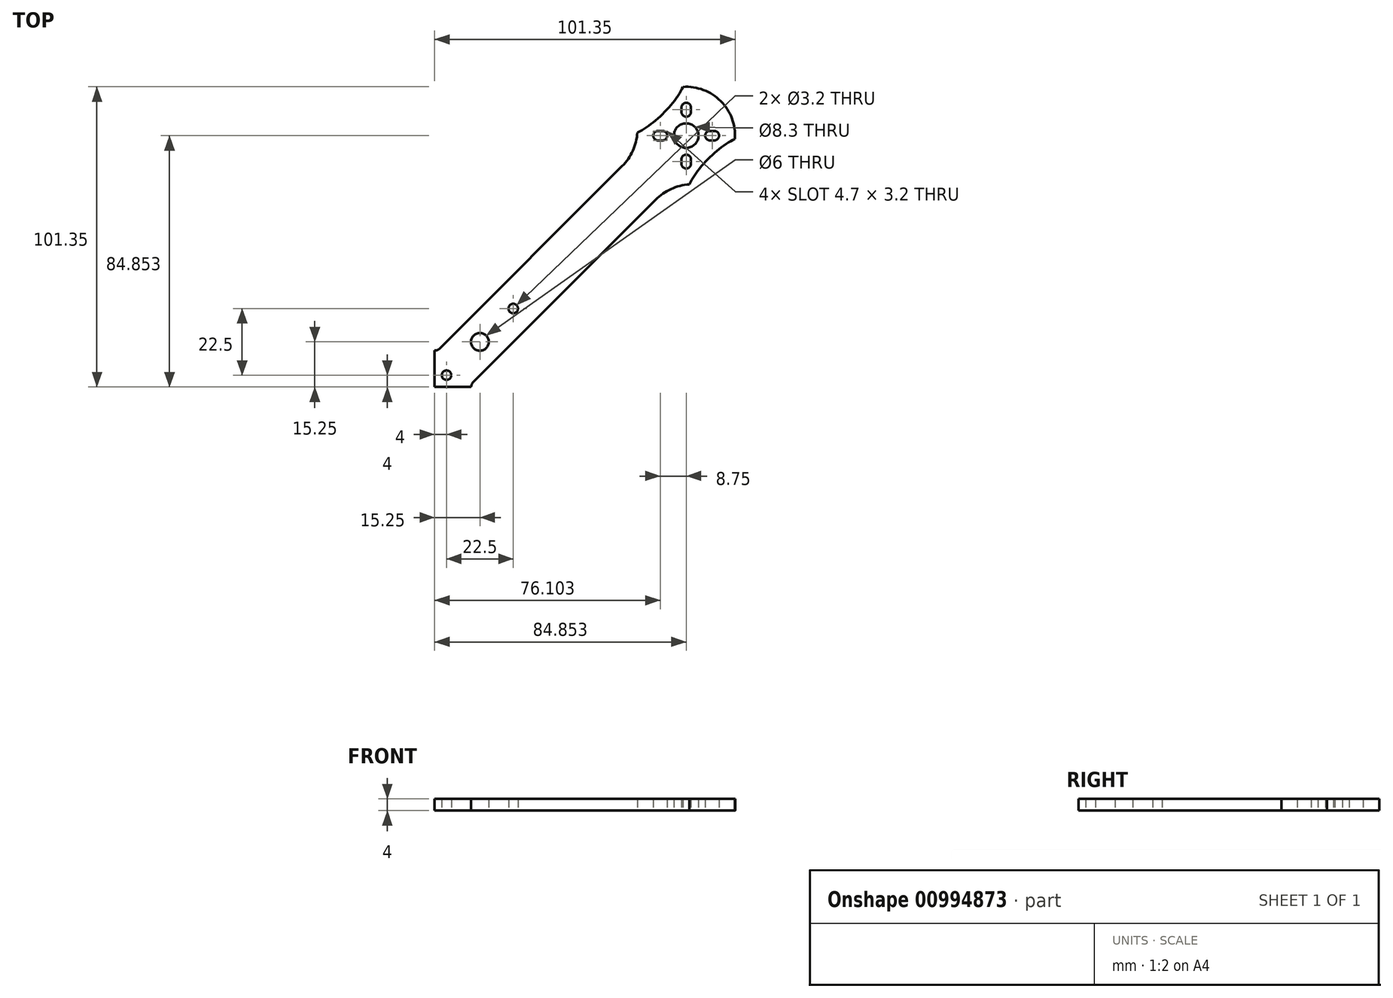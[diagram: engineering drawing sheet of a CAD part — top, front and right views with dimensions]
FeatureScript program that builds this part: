
annotation { "Feature Type Name" : "Feature", "Feature Type Description" : "" }
export const myFeature = defineFeature(function(context is Context, id is Id, definition is map)
    precondition{}
    {
        {
            var Q0;
            Q0=qCreatedBy(makeId("Top.planeOp"),FACE);
            var sketch = newSketch(context, id + "F0", { "sketchPlane" : qUnion([Q0])});
            skLineSegment(sketch, "E0.bottom", {"start": v(-18, 50) * mm, "end": v(18, 50) * mm, "construction": true});
            skLineSegment(sketch, "E0.top", {"start": v(-18, -50) * mm, "end": v(18, -50) * mm, "construction": true});
            skLineSegment(sketch, "E0.left", {"start": v(-18, 50) * mm, "end": v(-18, -50) * mm, "construction": true});
            skLineSegment(sketch, "E0.right", {"start": v(18, 50) * mm, "end": v(18, -50) * mm, "construction": true});
            skPoint(sketch, "E0.middle", {"position": v(0, 0) * mm});
            skLineSegment(sketch, "E1", {"start": v(0, 0) * mm, "end": v(15.25, 0) * mm, "construction": true});
            skLineSegment(sketch, "E2", {"start": v(15.25, 0) * mm, "end": v(15.25, 15.25) * mm, "construction": true});
            skCircle(sketch, "E3", {"center": v(15.25, 15.25) * mm, "radius": 3 * mm});
            skCircle(sketch, "E4.MirrorC", {"center": v(15.25, -15.25) * mm, "radius": 3 * mm, "construction": true});
            skCircle(sketch, "E5.MirrorC", {"center": v(-15.25, -15.25) * mm, "radius": 3 * mm, "construction": true});
            skCircle(sketch, "E6.MirrorC", {"center": v(-15.25, 15.25) * mm, "radius": 3 * mm, "construction": true});
            skLineSegment(sketch, "E7", {"start": v(0, 0) * mm, "end": v(84.85, 84.85) * mm, "construction": true});
            skLineSegment(sketch, "E8", {"start": v(84.85, 84.85) * mm, "end": v(79.2, 90.5) * mm});
            skLineSegment(sketch, "E9", {"start": v(79.2, 90.5) * mm, "end": v(90.5, 79.2) * mm});
            skLineSegment(sketch, "E10", {"start": v(90.5, 79.2) * mm, "end": v(11.31, 0) * mm});
            skLineSegment(sketch, "E11", {"start": v(11.31, 0) * mm, "end": v(0, 0) * mm});
            skLineSegment(sketch, "E12", {"start": v(79.2, 90.5) * mm, "end": v(0, 11.31) * mm});
            skLineSegment(sketch, "E13", {"start": v(0, 11.31) * mm, "end": v(0, 0) * mm});
            skCircle(sketch, "E14", {"center": v(84.85, 84.85) * mm, "radius": 16.5 * mm});
            skLineSegment(sketch, "E15", {"start": v(0, 0) * mm, "end": v(4, 0) * mm, "construction": true});
            skLineSegment(sketch, "E16", {"start": v(4, 0) * mm, "end": v(4, 4) * mm, "construction": true});
            skLineSegment(sketch, "E17", {"start": v(4, 4) * mm, "end": v(0, 4) * mm, "construction": true});
            skCircle(sketch, "E18", {"center": v(4, 4) * mm, "radius": 1.6 * mm});
            skLineSegment(sketch, "E19", {"start": v(84.85, 84.85) * mm, "end": v(91.57, 78.14) * mm, "construction": true});
            skCircle(sketch, "E20", {"center": v(91.57, 78.14) * mm, "radius": 1.6 * mm, "construction": true});
            skCircle(sketch, "E21", {"center": v(90.5, 79.2) * mm, "radius": 1.6 * mm, "construction": true});
            skLineSegment(sketch, "E22", {"start": v(92.7, 79.27) * mm, "end": v(91.64, 80.33) * mm, "construction": true});
            skLineSegment(sketch, "E23", {"start": v(90.45, 77) * mm, "end": v(89.37, 78.07) * mm, "construction": true});
            skLineSegment(sketch, "E24", {"start": v(84.85, 84.85) * mm, "end": v(89.12, 83.08) * mm, "construction": true});
            skLineSegment(sketch, "E25", {"start": v(84.85, 84.85) * mm, "end": v(84.85, 68.56) * mm, "construction": true});
            skCircle(sketch, "E26", {"center": v(84.85, 84.85) * mm, "radius": 4.15 * mm});
            skLineSegment(sketch, "E27.MirrorCS", {"start": v(94.35, 83.25) * mm, "end": v(92.85, 83.25) * mm});
            skCircle(sketch, "E28.MirrorC", {"center": v(92.85, 84.85) * mm, "radius": 1.6 * mm});
            skCircle(sketch, "E29.MirrorC", {"center": v(94.35, 84.85) * mm, "radius": 1.6 * mm});
            skLineSegment(sketch, "E30.MirrorCS", {"start": v(86.45, 75.35) * mm, "end": v(86.45, 76.85) * mm});
            skCircle(sketch, "E31.MirrorC", {"center": v(84.85, 75.35) * mm, "radius": 1.6 * mm});
            skCircle(sketch, "E32.MirrorC", {"center": v(84.85, 76.85) * mm, "radius": 1.6 * mm});
            skLineSegment(sketch, "E33.MirrorCS", {"start": v(83.25, 94.35) * mm, "end": v(83.25, 92.85) * mm});
            skCircle(sketch, "E34.MirrorC", {"center": v(84.85, 92.85) * mm, "radius": 1.6 * mm});
            skCircle(sketch, "E35.MirrorC", {"center": v(84.85, 94.35) * mm, "radius": 1.6 * mm});
            skCircle(sketch, "E36.MirrorC", {"center": v(76.85, 84.85) * mm, "radius": 1.6 * mm});
            skCircle(sketch, "E37.MirrorC", {"center": v(75.35, 84.85) * mm, "radius": 1.6 * mm});
            skLineSegment(sketch, "E38.MirrorCS", {"start": v(75.35, 86.45) * mm, "end": v(76.85, 86.45) * mm});
            skLineSegment(sketch, "E39", {"start": v(81.64, 84.85) * mm, "end": v(84.85, 84.85) * mm, "construction": true});
            skLineSegment(sketch, "E40", {"start": v(94.35, 84.85) * mm, "end": v(94.35, 86.45) * mm, "construction": true});
            skLineSegment(sketch, "E41", {"start": v(92.85, 84.85) * mm, "end": v(92.85, 86.45) * mm, "construction": true});
            skLineSegment(sketch, "E42", {"start": v(92.85, 86.45) * mm, "end": v(94.35, 86.45) * mm});
            skLineSegment(sketch, "E43.MirrorCS", {"start": v(84.85, 88.05) * mm, "end": v(91.57, 94.77) * mm, "construction": true});
            skLineSegment(sketch, "E44.MirrorCS", {"start": v(83.25, 76.85) * mm, "end": v(83.25, 75.35) * mm});
            skLineSegment(sketch, "E45.MirrorCS", {"start": v(76.85, 83.25) * mm, "end": v(75.35, 83.25) * mm});
            skLineSegment(sketch, "E46.MirrorCS", {"start": v(86.45, 92.85) * mm, "end": v(86.45, 94.35) * mm});
            skLineSegment(sketch, "E47", {"start": v(80.56, 89.14) * mm, "end": v(73.19, 96.52) * mm, "construction": true});
            skLineSegment(sketch, "E48", {"start": v(73.19, 96.52) * mm, "end": v(62.11, 85.45) * mm, "construction": true});
            skEllipse(sketch, "E49", {"center": v(73.19, 96.52) * mm, "majorRadius": 15.66 * mm, "minorRadius": 5.72 * mm, "majorAxis": v(-0.7, -0.7)});
            skEllipse(sketch, "E50.MirrorC", {"center": v(96.52, 73.19) * mm, "majorRadius": 15.66 * mm, "minorRadius": 5.72 * mm, "majorAxis": v(-0.7, -0.7)});
            skCircle(sketch, "E51", {"center": v(84.85, 84.85) * mm, "radius": 77.5 * mm, "construction": true});
            skCircle(sketch, "E52", {"center": v(26.5, 26.5) * mm, "radius": 1.6 * mm});
            skLineSegment(sketch, "E53", {"start": v(12.31, 0) * mm, "end": v(12.31, 1) * mm});
            skLineSegment(sketch, "E54", {"start": v(12.31, 0) * mm, "end": v(11.31, 0) * mm});
            skLineSegment(sketch, "E55", {"start": v(0, 12.31) * mm, "end": v(1, 12.31) * mm});
            skLineSegment(sketch, "E56", {"start": v(0, 12.31) * mm, "end": v(0, 11.31) * mm});
            skSolve(sketch);
        }
        {
            var Q0;
            Q0=makeQuery(id+"F0.imprint","IMPRINT",FACE,{"disambiguationData":[TD([[makeQuery(id+"F0.imprint","IMPRINT",EDGE,{"derivedFrom":sQuery(id+"F0.wireOp",EDGE,"E3")}),-1.0]])]});
            var Q1;
            {var subQ0=sQuery(id+"F0.wireOp",EDGE,"E30.MirrorCS");Q1=makeQuery(id+"F0.imprint","IMPRINT",FACE,{"disambiguationData":[TD([[makeQuery(id+"F0.imprint","IMPRINT",EDGE,{"derivedFrom":subQ0}),-1.0]])]});}
            var Q2;
            {var subQ18=sQuery(id+"F0.wireOp",EDGE,"E27.MirrorCS");Q2=makeQuery(id+"F0.imprint","IMPRINT",FACE,{"disambiguationData":[TD([[makeQuery(id+"F0.imprint","IMPRINT",EDGE,{"derivedFrom":subQ18}),1.0]])]});}
            var Q3;
            {var subQ2=sQuery(id+"F0.wireOp",EDGE,"E53");Q3=makeQuery(id+"F0.imprint","IMPRINT",FACE,{"disambiguationData":[TD([[makeQuery(id+"F0.imprint","IMPRINT",EDGE,{"derivedFrom":subQ2}),1.0]])]});}
            var Q4;
            {var subQ2=sQuery(id+"F0.wireOp",EDGE,"E55");Q4=makeQuery(id+"F0.imprint","IMPRINT",FACE,{"disambiguationData":[TD([[makeQuery(id+"F0.imprint","IMPRINT",EDGE,{"derivedFrom":subQ2}),-1.0]])]});}
            extrude(context, id + "F1", {"entities" : qUnion([Q0, Q1, Q2, Q3, Q4]), "depth" : 4 * mm, "offsetDistance" : 25 * mm});
        }
        {
            var Q0;
            Q0=makeQuery(id+"F1.opExtrude","SWEPT_EDGE",EDGE,{"disambiguationData":[OSD([sQuery(id+"F0.wireOp",EDGE,"E10"),sQuery(id+"F0.wireOp",EDGE,"E14")])]});
            var Q1;
            Q1=makeQuery(id+"F1.opExtrude","SWEPT_EDGE",EDGE,{"disambiguationData":[OSD([sQuery(id+"F0.wireOp",EDGE,"E12"),sQuery(id+"F0.wireOp",EDGE,"E14")])]});
            fillet(context, id + "F2", {"entities" : qUnion([Q0, Q1]), "radius" : 17.7 * mm, "tangentPropagation" : true, "defaultsChanged" : true, "vertexSettings" : [], "allowEdgeOverflow" : false});
        }
        {
            var Q0;
            Q0=makeQuery(id+"F1.opExtrude","SWEPT_EDGE",EDGE,{"disambiguationData":[OSD([sQuery(id+"F0.wireOp",EDGE,"E10"),sQuery(id+"F0.wireOp",EDGE,"E53")])]});
            var Q1;
            Q1=makeQuery(id+"F1.opExtrude","SWEPT_EDGE",EDGE,{"disambiguationData":[OSD([sQuery(id+"F0.wireOp",EDGE,"E12"),sQuery(id+"F0.wireOp",EDGE,"E55")])]});
            fillet(context, id + "F3", {"entities" : qUnion([Q0, Q1]), "tangentPropagation" : true, "radius" : 2.4 * mm, "defaultsChanged" : true, "vertexSettings" : [], "allowEdgeOverflow" : false});
        }
    });
